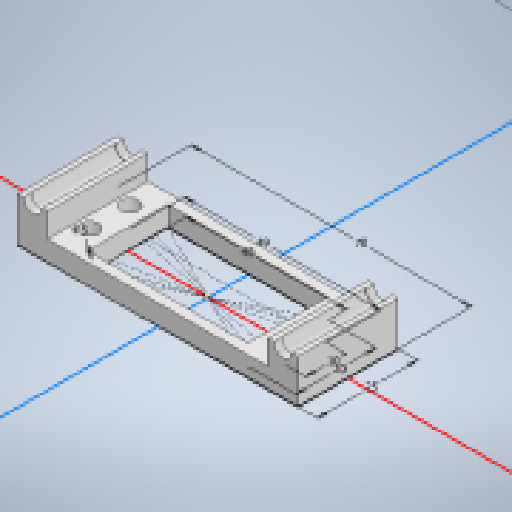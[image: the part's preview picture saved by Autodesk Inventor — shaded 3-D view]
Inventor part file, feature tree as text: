
AUTODESK INVENTOR PART (.ipt)
format: ipt  version: 2025.2 (Build 292293000, 293)  size: 185,856 bytes
history: native  units: mm
features: extrude x3, sketch x2, mirror x1
ambient origin geometry x8: Origin, YZ Plane, XZ Plane, XY Plane, X Axis, Y Axis, Z Axis, Center Point
bodies: Solid1 (feature_tree)
feature tree (6):
  sketch  "Sketch1"  dims[d0=10.0mm d1=49.0mm]
  extrude  "Extrusion1"  Depth=10.0mm
  sketch  "Sketch2"  dims[d2=4.5mm d3=5.0mm d4=0.0mm d5=25.0mm d6=70.0mm d7=20.0mm d8=40.0mm d9=5.0mm d10=7.5mm d12=6.0mm d13=5.0mm d14=0.0mm d18=0.2mm d19=2.0mm d20=0.0mm]
  extrude  "Extrusion2"  Depth=5.0mm TaperAngle=0.0deg
  extrude  "Extrusion4"  Depth=25.0mm
  mirror  "Mirror1"
